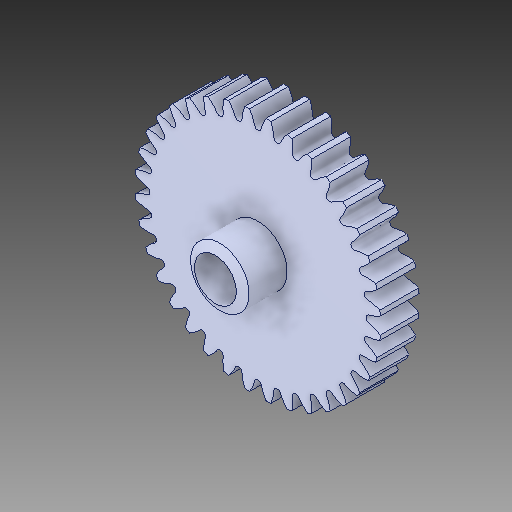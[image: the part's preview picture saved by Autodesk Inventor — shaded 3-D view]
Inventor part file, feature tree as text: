
AUTODESK INVENTOR PART (.ipt)
format: ipt  version: 2017 (Build 210142000, 142)  size: 409,600 bytes
history: native  units: in
note: dims shown in document units (in); Inventor stores cm internally (conversion verified against a paired STEP export)
features: chamfer x1
ambient origin geometry x8: Origin, YZ Plane, XZ Plane, XY Plane, X Axis, Y Axis, Z Axis, Center Point
bodies: Solid1 (feature_tree)
feature tree (1):
  chamfer  "Chamfer1"  [1 undecoded]
note: 1 required parameter value undecoded (feature->parameter linkage not recoverable at this tier; creation-order binding heuristic only, values carry confidence <= 0.55)
